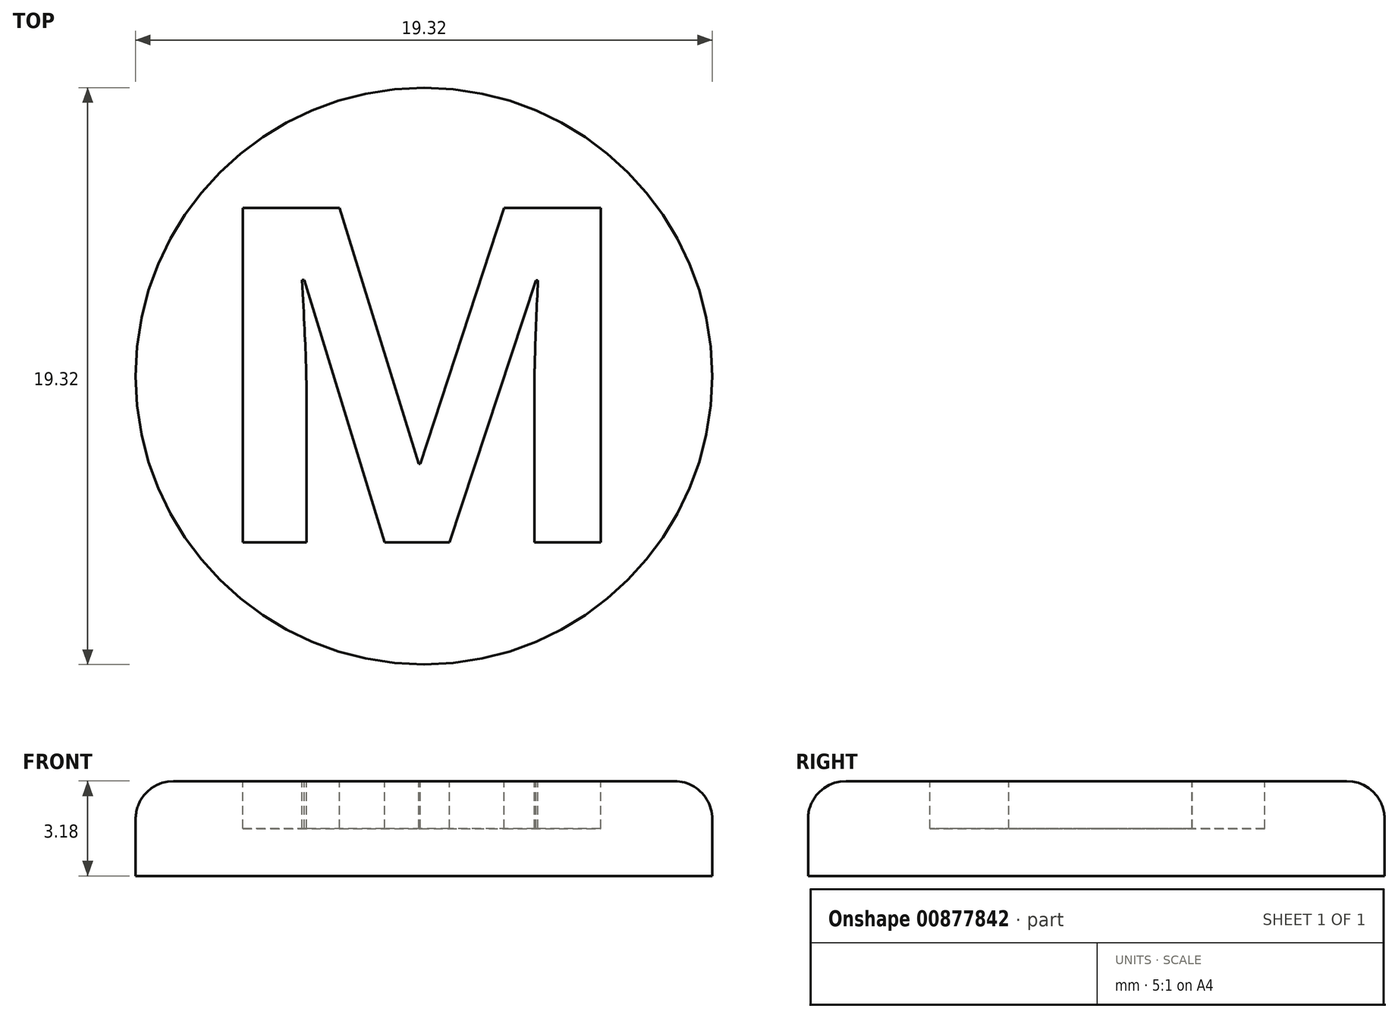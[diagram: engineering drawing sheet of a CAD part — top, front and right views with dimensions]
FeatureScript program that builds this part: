
annotation { "Feature Type Name" : "Feature", "Feature Type Description" : "" }
export const myFeature = defineFeature(function(context is Context, id is Id, definition is map)
    precondition{}
    {
        {
            var Q0;
            Q0=qCreatedBy(makeId("Top.planeOp"),FACE);
            var sketch = newSketch(context, id + "F0", { "sketchPlane" : qUnion([Q0])});
            skCircle(sketch, "E0", {"center": v(0, 0) * mm, "radius": 9.66 * mm});
            skSolve(sketch);
        }
        {
            var Q0;
            Q0 = qSketchRegion(id + "F0", true);
            extrude(context, id + "F1", {"entities" : qUnion([Q0]), "depth" : 3.17 * mm, "offsetDistance" : 25.4 * mm});
        }
        {
            var Q0;
            Q0=makeQuery(id+"F1.opExtrude","CAP_EDGE",EDGE,{"disambiguationData":[OSD([sQuery(id+"F0.wireOp",EDGE,"E0")])],"isStart":false});
            fillet(context, id + "F2", {"entities" : qUnion([Q0]), "radius" : 1.27 * mm, "tangentPropagation" : true, "allowEdgeOverflow" : false});
        }
        {
            var Q0;
            Q0=makeQuery(id+"F1.opExtrude","CAP_FACE",FACE,{"disambiguationData":[OSD([sQuery(id+"F0.wireOp",EDGE,"E0")])],"isStart":false});
            var sketch = newSketch(context, id + "F3", { "sketchPlane" : qUnion([Q0])});
            skText(sketch, "E1", { "text": "M", "fontName": "OpenSans-Bold.ttf"});
            const initialGuessF3  = {"E1": [-0.00747, -0.00557, 1, 0, 0.0113]};
            skSetInitialGuess(sketch, initialGuessF3);
            skSolve(sketch);
        }
        {
            var Q0;
            Q0 = qSketchRegion(id + "F3", true);
            extrude(context, id + "F4", {"entities" : qUnion([Q0]), "operationType" : NewBodyOperationType.REMOVE, "oppositeDirection" : true, "depth" : 1.59 * mm, "offsetDistance" : 25.4 * mm});
        }
    });
